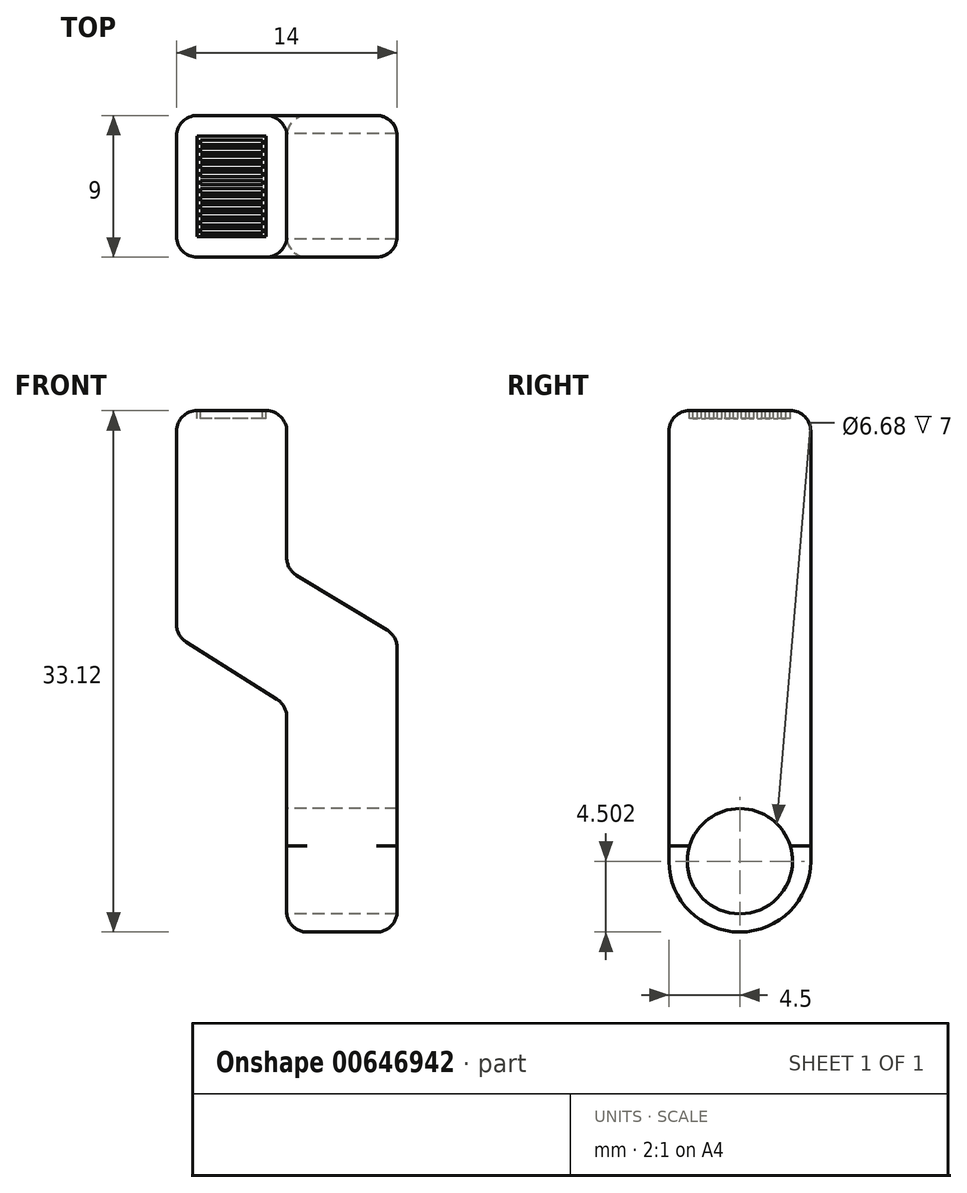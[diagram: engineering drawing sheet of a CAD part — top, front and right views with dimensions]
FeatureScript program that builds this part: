
annotation { "Feature Type Name" : "Feature", "Feature Type Description" : "" }
export const myFeature = defineFeature(function(context is Context, id is Id, definition is map)
    precondition{}
    {
        {
            var Q0;
            Q0=qCreatedBy(makeId("Right.planeOp"),FACE);
            var sketch = newSketch(context, id + "F0", { "sketchPlane" : qUnion([Q0])});
            skLineSegment(sketch, "E0.top", {"start": v(4.5, 14.3) * mm, "end": v(-4.5, 14.3) * mm});
            skLineSegment(sketch, "E0.left", {"start": v(4.5, -14.3) * mm, "end": v(4.5, 14.3) * mm});
            skLineSegment(sketch, "E0.right", {"start": v(-4.5, -14.3) * mm, "end": v(-4.5, 14.3) * mm});
            skPoint(sketch, "E0.middle", {"position": v(0, 0) * mm});
            skArc(sketch, "E1", {"start": v(-4.5, -14.3) * mm, "mid": v(0, -18.8) * mm, "end": v(4.5, -14.3) * mm});
            skCircle(sketch, "E2", {"center": v(0, -14.3) * mm, "radius": 3.34 * mm});
            skSolve(sketch);
        }
        {
            var Q0;
            Q0=makeQuery(id+"F0.imprint","IMPRINT",FACE,{"disambiguationData":[TD([[makeQuery(id+"F0.imprint","IMPRINT",EDGE,{"derivedFrom":sQuery(id+"F0.wireOp",EDGE,"E0.top")}),1.0]])]});
            var Q1;
            {var subQ0=sQuery(id+"F0.wireOp",EDGE,"e674e8e1-4115-40f2-bbbb-998aa0e4564f.121.0");Q1=makeQuery(id+"F0.imprint","IMPRINT",FACE,{"disambiguationData":[TD([[makeQuery(id+"F0.imprint","IMPRINT",EDGE,{"derivedFrom":subQ0}),1.0]])]});}
            var Q2;
            {var subQ0=sQuery(id+"F0.wireOp",EDGE,"e674e8e1-4115-40f2-bbbb-998aa0e4564f.120.0");Q2=makeQuery(id+"F0.imprint","IMPRINT",FACE,{"disambiguationData":[TD([[makeQuery(id+"F0.imprint","IMPRINT",EDGE,{"derivedFrom":subQ0}),1.0]])]});}
            var Q3;
            {var subQ0=sQuery(id+"F0.wireOp",EDGE,"e674e8e1-4115-40f2-bbbb-998aa0e4564f.118.0");Q3=makeQuery(id+"F0.imprint","IMPRINT",FACE,{"disambiguationData":[TD([[makeQuery(id+"F0.imprint","IMPRINT",EDGE,{"derivedFrom":subQ0}),1.0]])]});}
            var Q4;
            {var subQ0=sQuery(id+"F0.wireOp",EDGE,"e674e8e1-4115-40f2-bbbb-998aa0e4564f.119.0");Q4=makeQuery(id+"F0.imprint","IMPRINT",FACE,{"disambiguationData":[TD([[makeQuery(id+"F0.imprint","IMPRINT",EDGE,{"derivedFrom":subQ0}),1.0]])]});}
            var Q5;
            {var subQ0=sQuery(id+"F0.wireOp",EDGE,"e674e8e1-4115-40f2-bbbb-998aa0e4564f.117.0");Q5=makeQuery(id+"F0.imprint","IMPRINT",FACE,{"disambiguationData":[TD([[makeQuery(id+"F0.imprint","IMPRINT",EDGE,{"derivedFrom":subQ0}),1.0]])]});}
            var Q6;
            {var subQ0=sQuery(id+"F0.wireOp",EDGE,"e674e8e1-4115-40f2-bbbb-998aa0e4564f.115.0");Q6=makeQuery(id+"F0.imprint","IMPRINT",FACE,{"disambiguationData":[TD([[makeQuery(id+"F0.imprint","IMPRINT",EDGE,{"derivedFrom":subQ0}),1.0]])]});}
            var Q7;
            {var subQ0=sQuery(id+"F0.wireOp",EDGE,"e674e8e1-4115-40f2-bbbb-998aa0e4564f.116.0");Q7=makeQuery(id+"F0.imprint","IMPRINT",FACE,{"disambiguationData":[TD([[makeQuery(id+"F0.imprint","IMPRINT",EDGE,{"derivedFrom":subQ0}),1.0]])]});}
            var Q8;
            {var subQ0=sQuery(id+"F0.wireOp",EDGE,"e674e8e1-4115-40f2-bbbb-998aa0e4564f.114.0");Q8=makeQuery(id+"F0.imprint","IMPRINT",FACE,{"disambiguationData":[TD([[makeQuery(id+"F0.imprint","IMPRINT",EDGE,{"derivedFrom":subQ0}),1.0]])]});}
            var Q9;
            {var subQ0=sQuery(id+"F0.wireOp",EDGE,"e674e8e1-4115-40f2-bbbb-998aa0e4564f.113.0");Q9=makeQuery(id+"F0.imprint","IMPRINT",FACE,{"disambiguationData":[TD([[makeQuery(id+"F0.imprint","IMPRINT",EDGE,{"derivedFrom":subQ0}),1.0]])]});}
            var Q10;
            {var subQ0=sQuery(id+"F0.wireOp",EDGE,"e674e8e1-4115-40f2-bbbb-998aa0e4564f.112.0");Q10=makeQuery(id+"F0.imprint","IMPRINT",FACE,{"disambiguationData":[TD([[makeQuery(id+"F0.imprint","IMPRINT",EDGE,{"derivedFrom":subQ0}),1.0]])]});}
            var Q11;
            {var subQ0=sQuery(id+"F0.wireOp",EDGE,"e674e8e1-4115-40f2-bbbb-998aa0e4564f.111.0");Q11=makeQuery(id+"F0.imprint","IMPRINT",FACE,{"disambiguationData":[TD([[makeQuery(id+"F0.imprint","IMPRINT",EDGE,{"derivedFrom":subQ0}),1.0]])]});}
            var Q12;
            {var subQ0=sQuery(id+"F0.wireOp",EDGE,"e674e8e1-4115-40f2-bbbb-998aa0e4564f.108.0");Q12=makeQuery(id+"F0.imprint","IMPRINT",FACE,{"disambiguationData":[TD([[makeQuery(id+"F0.imprint","IMPRINT",EDGE,{"derivedFrom":subQ0}),1.0]])]});}
            var Q13;
            {var subQ0=sQuery(id+"F0.wireOp",EDGE,"e674e8e1-4115-40f2-bbbb-998aa0e4564f.106.0");Q13=makeQuery(id+"F0.imprint","IMPRINT",FACE,{"disambiguationData":[TD([[makeQuery(id+"F0.imprint","IMPRINT",EDGE,{"derivedFrom":subQ0}),1.0]])]});}
            var Q14;
            {var subQ0=sQuery(id+"F0.wireOp",EDGE,"e674e8e1-4115-40f2-bbbb-998aa0e4564f.107.0");Q14=makeQuery(id+"F0.imprint","IMPRINT",FACE,{"disambiguationData":[TD([[makeQuery(id+"F0.imprint","IMPRINT",EDGE,{"derivedFrom":subQ0}),1.0]])]});}
            var Q15;
            {var subQ0=sQuery(id+"F0.wireOp",EDGE,"e674e8e1-4115-40f2-bbbb-998aa0e4564f.110.0");Q15=makeQuery(id+"F0.imprint","IMPRINT",FACE,{"disambiguationData":[TD([[makeQuery(id+"F0.imprint","IMPRINT",EDGE,{"derivedFrom":subQ0}),1.0]])]});}
            var Q16;
            {var subQ0=sQuery(id+"F0.wireOp",EDGE,"e674e8e1-4115-40f2-bbbb-998aa0e4564f.109.0");Q16=makeQuery(id+"F0.imprint","IMPRINT",FACE,{"disambiguationData":[TD([[makeQuery(id+"F0.imprint","IMPRINT",EDGE,{"derivedFrom":subQ0}),1.0]])]});}
            var Q17;
            {var subQ0=sQuery(id+"F0.wireOp",EDGE,"e674e8e1-4115-40f2-bbbb-998aa0e4564f.103.0");Q17=makeQuery(id+"F0.imprint","IMPRINT",FACE,{"disambiguationData":[TD([[makeQuery(id+"F0.imprint","IMPRINT",EDGE,{"derivedFrom":subQ0}),1.0]])]});}
            var Q18;
            {var subQ0=sQuery(id+"F0.wireOp",EDGE,"e674e8e1-4115-40f2-bbbb-998aa0e4564f.100.0");Q18=makeQuery(id+"F0.imprint","IMPRINT",FACE,{"disambiguationData":[TD([[makeQuery(id+"F0.imprint","IMPRINT",EDGE,{"derivedFrom":subQ0}),1.0]])]});}
            var Q19;
            {var subQ0=sQuery(id+"F0.wireOp",EDGE,"e674e8e1-4115-40f2-bbbb-998aa0e4564f.98.0");Q19=makeQuery(id+"F0.imprint","IMPRINT",FACE,{"disambiguationData":[TD([[makeQuery(id+"F0.imprint","IMPRINT",EDGE,{"derivedFrom":subQ0}),1.0]])]});}
            var Q20;
            {var subQ0=sQuery(id+"F0.wireOp",EDGE,"e674e8e1-4115-40f2-bbbb-998aa0e4564f.99.0");Q20=makeQuery(id+"F0.imprint","IMPRINT",FACE,{"disambiguationData":[TD([[makeQuery(id+"F0.imprint","IMPRINT",EDGE,{"derivedFrom":subQ0}),1.0]])]});}
            var Q21;
            {var subQ0=sQuery(id+"F0.wireOp",EDGE,"e674e8e1-4115-40f2-bbbb-998aa0e4564f.101.0");Q21=makeQuery(id+"F0.imprint","IMPRINT",FACE,{"disambiguationData":[TD([[makeQuery(id+"F0.imprint","IMPRINT",EDGE,{"derivedFrom":subQ0}),1.0]])]});}
            var Q22;
            {var subQ0=sQuery(id+"F0.wireOp",EDGE,"e674e8e1-4115-40f2-bbbb-998aa0e4564f.102.0");Q22=makeQuery(id+"F0.imprint","IMPRINT",FACE,{"disambiguationData":[TD([[makeQuery(id+"F0.imprint","IMPRINT",EDGE,{"derivedFrom":subQ0}),1.0]])]});}
            var Q23;
            {var subQ0=sQuery(id+"F0.wireOp",EDGE,"e674e8e1-4115-40f2-bbbb-998aa0e4564f.104.0");Q23=makeQuery(id+"F0.imprint","IMPRINT",FACE,{"disambiguationData":[TD([[makeQuery(id+"F0.imprint","IMPRINT",EDGE,{"derivedFrom":subQ0}),1.0]])]});}
            var Q24;
            {var subQ0=sQuery(id+"F0.wireOp",EDGE,"e674e8e1-4115-40f2-bbbb-998aa0e4564f.105.0");Q24=makeQuery(id+"F0.imprint","IMPRINT",FACE,{"disambiguationData":[TD([[makeQuery(id+"F0.imprint","IMPRINT",EDGE,{"derivedFrom":subQ0}),1.0]])]});}
            var Q25;
            {var subQ0=sQuery(id+"F0.wireOp",EDGE,"e674e8e1-4115-40f2-bbbb-998aa0e4564f.92.0");Q25=makeQuery(id+"F0.imprint","IMPRINT",FACE,{"disambiguationData":[TD([[makeQuery(id+"F0.imprint","IMPRINT",EDGE,{"derivedFrom":subQ0}),1.0]])]});}
            var Q26;
            {var subQ0=sQuery(id+"F0.wireOp",EDGE,"e674e8e1-4115-40f2-bbbb-998aa0e4564f.91.0");Q26=makeQuery(id+"F0.imprint","IMPRINT",FACE,{"disambiguationData":[TD([[makeQuery(id+"F0.imprint","IMPRINT",EDGE,{"derivedFrom":subQ0}),1.0]])]});}
            var Q27;
            {var subQ0=sQuery(id+"F0.wireOp",EDGE,"e674e8e1-4115-40f2-bbbb-998aa0e4564f.93.0");Q27=makeQuery(id+"F0.imprint","IMPRINT",FACE,{"disambiguationData":[TD([[makeQuery(id+"F0.imprint","IMPRINT",EDGE,{"derivedFrom":subQ0}),1.0]])]});}
            var Q28;
            {var subQ0=sQuery(id+"F0.wireOp",EDGE,"e674e8e1-4115-40f2-bbbb-998aa0e4564f.94.0");Q28=makeQuery(id+"F0.imprint","IMPRINT",FACE,{"disambiguationData":[TD([[makeQuery(id+"F0.imprint","IMPRINT",EDGE,{"derivedFrom":subQ0}),1.0]])]});}
            var Q29;
            {var subQ0=sQuery(id+"F0.wireOp",EDGE,"e674e8e1-4115-40f2-bbbb-998aa0e4564f.95.0");Q29=makeQuery(id+"F0.imprint","IMPRINT",FACE,{"disambiguationData":[TD([[makeQuery(id+"F0.imprint","IMPRINT",EDGE,{"derivedFrom":subQ0}),1.0]])]});}
            var Q30;
            {var subQ0=sQuery(id+"F0.wireOp",EDGE,"e674e8e1-4115-40f2-bbbb-998aa0e4564f.96.0");Q30=makeQuery(id+"F0.imprint","IMPRINT",FACE,{"disambiguationData":[TD([[makeQuery(id+"F0.imprint","IMPRINT",EDGE,{"derivedFrom":subQ0}),1.0]])]});}
            var Q31;
            {var subQ0=sQuery(id+"F0.wireOp",EDGE,"e674e8e1-4115-40f2-bbbb-998aa0e4564f.97.0");Q31=makeQuery(id+"F0.imprint","IMPRINT",FACE,{"disambiguationData":[TD([[makeQuery(id+"F0.imprint","IMPRINT",EDGE,{"derivedFrom":subQ0}),1.0]])]});}
            var Q32;
            {var subQ0=sQuery(id+"F0.wireOp",EDGE,"e674e8e1-4115-40f2-bbbb-998aa0e4564f.90.0");Q32=makeQuery(id+"F0.imprint","IMPRINT",FACE,{"disambiguationData":[TD([[makeQuery(id+"F0.imprint","IMPRINT",EDGE,{"derivedFrom":subQ0}),1.0]])]});}
            var Q33;
            {var subQ0=sQuery(id+"F0.wireOp",EDGE,"e674e8e1-4115-40f2-bbbb-998aa0e4564f.89.0");Q33=makeQuery(id+"F0.imprint","IMPRINT",FACE,{"disambiguationData":[TD([[makeQuery(id+"F0.imprint","IMPRINT",EDGE,{"derivedFrom":subQ0}),1.0]])]});}
            var Q34;
            {var subQ0=sQuery(id+"F0.wireOp",EDGE,"e674e8e1-4115-40f2-bbbb-998aa0e4564f.88.0");Q34=makeQuery(id+"F0.imprint","IMPRINT",FACE,{"disambiguationData":[TD([[makeQuery(id+"F0.imprint","IMPRINT",EDGE,{"derivedFrom":subQ0}),1.0]])]});}
            var Q35;
            {var subQ0=sQuery(id+"F0.wireOp",EDGE,"e674e8e1-4115-40f2-bbbb-998aa0e4564f.87.0");Q35=makeQuery(id+"F0.imprint","IMPRINT",FACE,{"disambiguationData":[TD([[makeQuery(id+"F0.imprint","IMPRINT",EDGE,{"derivedFrom":subQ0}),1.0]])]});}
            var Q36;
            {var subQ0=sQuery(id+"F0.wireOp",EDGE,"e674e8e1-4115-40f2-bbbb-998aa0e4564f.86.0");Q36=makeQuery(id+"F0.imprint","IMPRINT",FACE,{"disambiguationData":[TD([[makeQuery(id+"F0.imprint","IMPRINT",EDGE,{"derivedFrom":subQ0}),1.0]])]});}
            var Q37;
            {var subQ0=sQuery(id+"F0.wireOp",EDGE,"e674e8e1-4115-40f2-bbbb-998aa0e4564f.85.0");Q37=makeQuery(id+"F0.imprint","IMPRINT",FACE,{"disambiguationData":[TD([[makeQuery(id+"F0.imprint","IMPRINT",EDGE,{"derivedFrom":subQ0}),1.0]])]});}
            var Q38;
            {var subQ0=sQuery(id+"F0.wireOp",EDGE,"e674e8e1-4115-40f2-bbbb-998aa0e4564f.84.0");Q38=makeQuery(id+"F0.imprint","IMPRINT",FACE,{"disambiguationData":[TD([[makeQuery(id+"F0.imprint","IMPRINT",EDGE,{"derivedFrom":subQ0}),1.0]])]});}
            var Q39;
            {var subQ0=sQuery(id+"F0.wireOp",EDGE,"e674e8e1-4115-40f2-bbbb-998aa0e4564f.83.0");Q39=makeQuery(id+"F0.imprint","IMPRINT",FACE,{"disambiguationData":[TD([[makeQuery(id+"F0.imprint","IMPRINT",EDGE,{"derivedFrom":subQ0}),1.0]])]});}
            var Q40;
            {var subQ0=sQuery(id+"F0.wireOp",EDGE,"e674e8e1-4115-40f2-bbbb-998aa0e4564f.82.0");Q40=makeQuery(id+"F0.imprint","IMPRINT",FACE,{"disambiguationData":[TD([[makeQuery(id+"F0.imprint","IMPRINT",EDGE,{"derivedFrom":subQ0}),1.0]])]});}
            var Q41;
            {var subQ0=sQuery(id+"F0.wireOp",EDGE,"e674e8e1-4115-40f2-bbbb-998aa0e4564f.81.0");Q41=makeQuery(id+"F0.imprint","IMPRINT",FACE,{"disambiguationData":[TD([[makeQuery(id+"F0.imprint","IMPRINT",EDGE,{"derivedFrom":subQ0}),1.0]])]});}
            var Q42;
            {var subQ0=sQuery(id+"F0.wireOp",EDGE,"e674e8e1-4115-40f2-bbbb-998aa0e4564f.80.0");Q42=makeQuery(id+"F0.imprint","IMPRINT",FACE,{"disambiguationData":[TD([[makeQuery(id+"F0.imprint","IMPRINT",EDGE,{"derivedFrom":subQ0}),1.0]])]});}
            var Q43;
            {var subQ0=sQuery(id+"F0.wireOp",EDGE,"e674e8e1-4115-40f2-bbbb-998aa0e4564f.79.0");Q43=makeQuery(id+"F0.imprint","IMPRINT",FACE,{"disambiguationData":[TD([[makeQuery(id+"F0.imprint","IMPRINT",EDGE,{"derivedFrom":subQ0}),1.0]])]});}
            var Q44;
            {var subQ0=sQuery(id+"F0.wireOp",EDGE,"e674e8e1-4115-40f2-bbbb-998aa0e4564f.78.0");Q44=makeQuery(id+"F0.imprint","IMPRINT",FACE,{"disambiguationData":[TD([[makeQuery(id+"F0.imprint","IMPRINT",EDGE,{"derivedFrom":subQ0}),1.0]])]});}
            var Q45;
            {var subQ0=sQuery(id+"F0.wireOp",EDGE,"e674e8e1-4115-40f2-bbbb-998aa0e4564f.77.0");Q45=makeQuery(id+"F0.imprint","IMPRINT",FACE,{"disambiguationData":[TD([[makeQuery(id+"F0.imprint","IMPRINT",EDGE,{"derivedFrom":subQ0}),1.0]])]});}
            var Q46;
            {var subQ0=sQuery(id+"F0.wireOp",EDGE,"e674e8e1-4115-40f2-bbbb-998aa0e4564f.76.0");Q46=makeQuery(id+"F0.imprint","IMPRINT",FACE,{"disambiguationData":[TD([[makeQuery(id+"F0.imprint","IMPRINT",EDGE,{"derivedFrom":subQ0}),1.0]])]});}
            var Q47;
            {var subQ0=sQuery(id+"F0.wireOp",EDGE,"e674e8e1-4115-40f2-bbbb-998aa0e4564f.75.0");Q47=makeQuery(id+"F0.imprint","IMPRINT",FACE,{"disambiguationData":[TD([[makeQuery(id+"F0.imprint","IMPRINT",EDGE,{"derivedFrom":subQ0}),1.0]])]});}
            var Q48;
            {var subQ0=sQuery(id+"F0.wireOp",EDGE,"e674e8e1-4115-40f2-bbbb-998aa0e4564f.74.0");Q48=makeQuery(id+"F0.imprint","IMPRINT",FACE,{"disambiguationData":[TD([[makeQuery(id+"F0.imprint","IMPRINT",EDGE,{"derivedFrom":subQ0}),1.0]])]});}
            var Q49;
            {var subQ0=sQuery(id+"F0.wireOp",EDGE,"e674e8e1-4115-40f2-bbbb-998aa0e4564f.73.0");Q49=makeQuery(id+"F0.imprint","IMPRINT",FACE,{"disambiguationData":[TD([[makeQuery(id+"F0.imprint","IMPRINT",EDGE,{"derivedFrom":subQ0}),1.0]])]});}
            var Q50;
            {var subQ0=sQuery(id+"F0.wireOp",EDGE,"e674e8e1-4115-40f2-bbbb-998aa0e4564f.72.0");Q50=makeQuery(id+"F0.imprint","IMPRINT",FACE,{"disambiguationData":[TD([[makeQuery(id+"F0.imprint","IMPRINT",EDGE,{"derivedFrom":subQ0}),1.0]])]});}
            var Q51;
            {var subQ0=sQuery(id+"F0.wireOp",EDGE,"e674e8e1-4115-40f2-bbbb-998aa0e4564f.71.0");Q51=makeQuery(id+"F0.imprint","IMPRINT",FACE,{"disambiguationData":[TD([[makeQuery(id+"F0.imprint","IMPRINT",EDGE,{"derivedFrom":subQ0}),1.0]])]});}
            var Q52;
            {var subQ0=sQuery(id+"F0.wireOp",EDGE,"e674e8e1-4115-40f2-bbbb-998aa0e4564f.70.0");Q52=makeQuery(id+"F0.imprint","IMPRINT",FACE,{"disambiguationData":[TD([[makeQuery(id+"F0.imprint","IMPRINT",EDGE,{"derivedFrom":subQ0}),1.0]])]});}
            var Q53;
            {var subQ0=sQuery(id+"F0.wireOp",EDGE,"e674e8e1-4115-40f2-bbbb-998aa0e4564f.69.0");Q53=makeQuery(id+"F0.imprint","IMPRINT",FACE,{"disambiguationData":[TD([[makeQuery(id+"F0.imprint","IMPRINT",EDGE,{"derivedFrom":subQ0}),1.0]])]});}
            var Q54;
            {var subQ0=sQuery(id+"F0.wireOp",EDGE,"e674e8e1-4115-40f2-bbbb-998aa0e4564f.68.0");Q54=makeQuery(id+"F0.imprint","IMPRINT",FACE,{"disambiguationData":[TD([[makeQuery(id+"F0.imprint","IMPRINT",EDGE,{"derivedFrom":subQ0}),1.0]])]});}
            var Q55;
            {var subQ0=sQuery(id+"F0.wireOp",EDGE,"e674e8e1-4115-40f2-bbbb-998aa0e4564f.67.0");Q55=makeQuery(id+"F0.imprint","IMPRINT",FACE,{"disambiguationData":[TD([[makeQuery(id+"F0.imprint","IMPRINT",EDGE,{"derivedFrom":subQ0}),1.0]])]});}
            var Q56;
            {var subQ0=sQuery(id+"F0.wireOp",EDGE,"e674e8e1-4115-40f2-bbbb-998aa0e4564f.66.0");Q56=makeQuery(id+"F0.imprint","IMPRINT",FACE,{"disambiguationData":[TD([[makeQuery(id+"F0.imprint","IMPRINT",EDGE,{"derivedFrom":subQ0}),1.0]])]});}
            var Q57;
            {var subQ0=sQuery(id+"F0.wireOp",EDGE,"e674e8e1-4115-40f2-bbbb-998aa0e4564f.65.0");Q57=makeQuery(id+"F0.imprint","IMPRINT",FACE,{"disambiguationData":[TD([[makeQuery(id+"F0.imprint","IMPRINT",EDGE,{"derivedFrom":subQ0}),1.0]])]});}
            var Q58;
            {var subQ0=sQuery(id+"F0.wireOp",EDGE,"e674e8e1-4115-40f2-bbbb-998aa0e4564f.64.0");Q58=makeQuery(id+"F0.imprint","IMPRINT",FACE,{"disambiguationData":[TD([[makeQuery(id+"F0.imprint","IMPRINT",EDGE,{"derivedFrom":subQ0}),1.0]])]});}
            var Q59;
            {var subQ0=sQuery(id+"F0.wireOp",EDGE,"e674e8e1-4115-40f2-bbbb-998aa0e4564f.62.0");Q59=makeQuery(id+"F0.imprint","IMPRINT",FACE,{"disambiguationData":[TD([[makeQuery(id+"F0.imprint","IMPRINT",EDGE,{"derivedFrom":subQ0}),1.0]])]});}
            var Q60;
            {var subQ0=sQuery(id+"F0.wireOp",EDGE,"e674e8e1-4115-40f2-bbbb-998aa0e4564f.63.0");Q60=makeQuery(id+"F0.imprint","IMPRINT",FACE,{"disambiguationData":[TD([[makeQuery(id+"F0.imprint","IMPRINT",EDGE,{"derivedFrom":subQ0}),1.0]])]});}
            var Q61;
            {var subQ0=sQuery(id+"F0.wireOp",EDGE,"e674e8e1-4115-40f2-bbbb-998aa0e4564f.61.0");Q61=makeQuery(id+"F0.imprint","IMPRINT",FACE,{"disambiguationData":[TD([[makeQuery(id+"F0.imprint","IMPRINT",EDGE,{"derivedFrom":subQ0}),1.0]])]});}
            var Q62;
            {var subQ0=sQuery(id+"F0.wireOp",EDGE,"e674e8e1-4115-40f2-bbbb-998aa0e4564f.58.0");Q62=makeQuery(id+"F0.imprint","IMPRINT",FACE,{"disambiguationData":[TD([[makeQuery(id+"F0.imprint","IMPRINT",EDGE,{"derivedFrom":subQ0}),1.0]])]});}
            var Q63;
            {var subQ0=sQuery(id+"F0.wireOp",EDGE,"e674e8e1-4115-40f2-bbbb-998aa0e4564f.59.0");Q63=makeQuery(id+"F0.imprint","IMPRINT",FACE,{"disambiguationData":[TD([[makeQuery(id+"F0.imprint","IMPRINT",EDGE,{"derivedFrom":subQ0}),1.0]])]});}
            var Q64;
            {var subQ0=sQuery(id+"F0.wireOp",EDGE,"e674e8e1-4115-40f2-bbbb-998aa0e4564f.60.0");Q64=makeQuery(id+"F0.imprint","IMPRINT",FACE,{"disambiguationData":[TD([[makeQuery(id+"F0.imprint","IMPRINT",EDGE,{"derivedFrom":subQ0}),1.0]])]});}
            var Q65;
            {var subQ0=sQuery(id+"F0.wireOp",EDGE,"e674e8e1-4115-40f2-bbbb-998aa0e4564f.56.0");Q65=makeQuery(id+"F0.imprint","IMPRINT",FACE,{"disambiguationData":[TD([[makeQuery(id+"F0.imprint","IMPRINT",EDGE,{"derivedFrom":subQ0}),1.0]])]});}
            var Q66;
            {var subQ0=sQuery(id+"F0.wireOp",EDGE,"e674e8e1-4115-40f2-bbbb-998aa0e4564f.57.0");Q66=makeQuery(id+"F0.imprint","IMPRINT",FACE,{"disambiguationData":[TD([[makeQuery(id+"F0.imprint","IMPRINT",EDGE,{"derivedFrom":subQ0}),1.0]])]});}
            var Q67;
            {var subQ0=sQuery(id+"F0.wireOp",EDGE,"e674e8e1-4115-40f2-bbbb-998aa0e4564f.55.0");Q67=makeQuery(id+"F0.imprint","IMPRINT",FACE,{"disambiguationData":[TD([[makeQuery(id+"F0.imprint","IMPRINT",EDGE,{"derivedFrom":subQ0}),1.0]])]});}
            var Q68;
            {var subQ0=sQuery(id+"F0.wireOp",EDGE,"e674e8e1-4115-40f2-bbbb-998aa0e4564f.54.0");Q68=makeQuery(id+"F0.imprint","IMPRINT",FACE,{"disambiguationData":[TD([[makeQuery(id+"F0.imprint","IMPRINT",EDGE,{"derivedFrom":subQ0}),1.0]])]});}
            var Q69;
            {var subQ0=sQuery(id+"F0.wireOp",EDGE,"e674e8e1-4115-40f2-bbbb-998aa0e4564f.53.0");Q69=makeQuery(id+"F0.imprint","IMPRINT",FACE,{"disambiguationData":[TD([[makeQuery(id+"F0.imprint","IMPRINT",EDGE,{"derivedFrom":subQ0}),1.0]])]});}
            var Q70;
            {var subQ0=sQuery(id+"F0.wireOp",EDGE,"e674e8e1-4115-40f2-bbbb-998aa0e4564f.52.0");Q70=makeQuery(id+"F0.imprint","IMPRINT",FACE,{"disambiguationData":[TD([[makeQuery(id+"F0.imprint","IMPRINT",EDGE,{"derivedFrom":subQ0}),1.0]])]});}
            var Q71;
            {var subQ0=sQuery(id+"F0.wireOp",EDGE,"e674e8e1-4115-40f2-bbbb-998aa0e4564f.51.0");Q71=makeQuery(id+"F0.imprint","IMPRINT",FACE,{"disambiguationData":[TD([[makeQuery(id+"F0.imprint","IMPRINT",EDGE,{"derivedFrom":subQ0}),1.0]])]});}
            var Q72;
            {var subQ0=sQuery(id+"F0.wireOp",EDGE,"e674e8e1-4115-40f2-bbbb-998aa0e4564f.50.0");Q72=makeQuery(id+"F0.imprint","IMPRINT",FACE,{"disambiguationData":[TD([[makeQuery(id+"F0.imprint","IMPRINT",EDGE,{"derivedFrom":subQ0}),1.0]])]});}
            var Q73;
            {var subQ0=sQuery(id+"F0.wireOp",EDGE,"e674e8e1-4115-40f2-bbbb-998aa0e4564f.49.0");Q73=makeQuery(id+"F0.imprint","IMPRINT",FACE,{"disambiguationData":[TD([[makeQuery(id+"F0.imprint","IMPRINT",EDGE,{"derivedFrom":subQ0}),1.0]])]});}
            var Q74;
            {var subQ0=sQuery(id+"F0.wireOp",EDGE,"e674e8e1-4115-40f2-bbbb-998aa0e4564f.48.0");Q74=makeQuery(id+"F0.imprint","IMPRINT",FACE,{"disambiguationData":[TD([[makeQuery(id+"F0.imprint","IMPRINT",EDGE,{"derivedFrom":subQ0}),1.0]])]});}
            var Q75;
            {var subQ0=sQuery(id+"F0.wireOp",EDGE,"e674e8e1-4115-40f2-bbbb-998aa0e4564f.47.0");Q75=makeQuery(id+"F0.imprint","IMPRINT",FACE,{"disambiguationData":[TD([[makeQuery(id+"F0.imprint","IMPRINT",EDGE,{"derivedFrom":subQ0}),1.0]])]});}
            var Q76;
            {var subQ0=sQuery(id+"F0.wireOp",EDGE,"e674e8e1-4115-40f2-bbbb-998aa0e4564f.44.0");Q76=makeQuery(id+"F0.imprint","IMPRINT",FACE,{"disambiguationData":[TD([[makeQuery(id+"F0.imprint","IMPRINT",EDGE,{"derivedFrom":subQ0}),1.0]])]});}
            var Q77;
            {var subQ0=sQuery(id+"F0.wireOp",EDGE,"e674e8e1-4115-40f2-bbbb-998aa0e4564f.46.0");Q77=makeQuery(id+"F0.imprint","IMPRINT",FACE,{"disambiguationData":[TD([[makeQuery(id+"F0.imprint","IMPRINT",EDGE,{"derivedFrom":subQ0}),1.0]])]});}
            var Q78;
            {var subQ0=sQuery(id+"F0.wireOp",EDGE,"e674e8e1-4115-40f2-bbbb-998aa0e4564f.43.0");Q78=makeQuery(id+"F0.imprint","IMPRINT",FACE,{"disambiguationData":[TD([[makeQuery(id+"F0.imprint","IMPRINT",EDGE,{"derivedFrom":subQ0}),1.0]])]});}
            var Q79;
            {var subQ0=sQuery(id+"F0.wireOp",EDGE,"e674e8e1-4115-40f2-bbbb-998aa0e4564f.45.0");Q79=makeQuery(id+"F0.imprint","IMPRINT",FACE,{"disambiguationData":[TD([[makeQuery(id+"F0.imprint","IMPRINT",EDGE,{"derivedFrom":subQ0}),1.0]])]});}
            var Q80;
            {var subQ0=sQuery(id+"F0.wireOp",EDGE,"e674e8e1-4115-40f2-bbbb-998aa0e4564f.42.0");Q80=makeQuery(id+"F0.imprint","IMPRINT",FACE,{"disambiguationData":[TD([[makeQuery(id+"F0.imprint","IMPRINT",EDGE,{"derivedFrom":subQ0}),1.0]])]});}
            var Q81;
            {var subQ0=sQuery(id+"F0.wireOp",EDGE,"e674e8e1-4115-40f2-bbbb-998aa0e4564f.41.0");Q81=makeQuery(id+"F0.imprint","IMPRINT",FACE,{"disambiguationData":[TD([[makeQuery(id+"F0.imprint","IMPRINT",EDGE,{"derivedFrom":subQ0}),1.0]])]});}
            var Q82;
            {var subQ0=sQuery(id+"F0.wireOp",EDGE,"e674e8e1-4115-40f2-bbbb-998aa0e4564f.40.0");Q82=makeQuery(id+"F0.imprint","IMPRINT",FACE,{"disambiguationData":[TD([[makeQuery(id+"F0.imprint","IMPRINT",EDGE,{"derivedFrom":subQ0}),1.0]])]});}
            var Q83;
            {var subQ0=sQuery(id+"F0.wireOp",EDGE,"e674e8e1-4115-40f2-bbbb-998aa0e4564f.39.0");Q83=makeQuery(id+"F0.imprint","IMPRINT",FACE,{"disambiguationData":[TD([[makeQuery(id+"F0.imprint","IMPRINT",EDGE,{"derivedFrom":subQ0}),1.0]])]});}
            var Q84;
            {var subQ0=sQuery(id+"F0.wireOp",EDGE,"e674e8e1-4115-40f2-bbbb-998aa0e4564f.35.0");Q84=makeQuery(id+"F0.imprint","IMPRINT",FACE,{"disambiguationData":[TD([[makeQuery(id+"F0.imprint","IMPRINT",EDGE,{"derivedFrom":subQ0}),1.0]])]});}
            var Q85;
            {var subQ0=sQuery(id+"F0.wireOp",EDGE,"e674e8e1-4115-40f2-bbbb-998aa0e4564f.38.0");Q85=makeQuery(id+"F0.imprint","IMPRINT",FACE,{"disambiguationData":[TD([[makeQuery(id+"F0.imprint","IMPRINT",EDGE,{"derivedFrom":subQ0}),1.0]])]});}
            var Q86;
            {var subQ0=sQuery(id+"F0.wireOp",EDGE,"e674e8e1-4115-40f2-bbbb-998aa0e4564f.34.0");Q86=makeQuery(id+"F0.imprint","IMPRINT",FACE,{"disambiguationData":[TD([[makeQuery(id+"F0.imprint","IMPRINT",EDGE,{"derivedFrom":subQ0}),1.0]])]});}
            var Q87;
            {var subQ0=sQuery(id+"F0.wireOp",EDGE,"e674e8e1-4115-40f2-bbbb-998aa0e4564f.37.0");Q87=makeQuery(id+"F0.imprint","IMPRINT",FACE,{"disambiguationData":[TD([[makeQuery(id+"F0.imprint","IMPRINT",EDGE,{"derivedFrom":subQ0}),1.0]])]});}
            var Q88;
            {var subQ0=sQuery(id+"F0.wireOp",EDGE,"e674e8e1-4115-40f2-bbbb-998aa0e4564f.36.0");Q88=makeQuery(id+"F0.imprint","IMPRINT",FACE,{"disambiguationData":[TD([[makeQuery(id+"F0.imprint","IMPRINT",EDGE,{"derivedFrom":subQ0}),1.0]])]});}
            var Q89;
            {var subQ0=sQuery(id+"F0.wireOp",EDGE,"e674e8e1-4115-40f2-bbbb-998aa0e4564f.33.0");Q89=makeQuery(id+"F0.imprint","IMPRINT",FACE,{"disambiguationData":[TD([[makeQuery(id+"F0.imprint","IMPRINT",EDGE,{"derivedFrom":subQ0}),1.0]])]});}
            var Q90;
            {var subQ0=sQuery(id+"F0.wireOp",EDGE,"e674e8e1-4115-40f2-bbbb-998aa0e4564f.32.0");Q90=makeQuery(id+"F0.imprint","IMPRINT",FACE,{"disambiguationData":[TD([[makeQuery(id+"F0.imprint","IMPRINT",EDGE,{"derivedFrom":subQ0}),1.0]])]});}
            var Q91;
            {var subQ0=sQuery(id+"F0.wireOp",EDGE,"e674e8e1-4115-40f2-bbbb-998aa0e4564f.30.0");Q91=makeQuery(id+"F0.imprint","IMPRINT",FACE,{"disambiguationData":[TD([[makeQuery(id+"F0.imprint","IMPRINT",EDGE,{"derivedFrom":subQ0}),1.0]])]});}
            var Q92;
            {var subQ0=sQuery(id+"F0.wireOp",EDGE,"e674e8e1-4115-40f2-bbbb-998aa0e4564f.31.0");Q92=makeQuery(id+"F0.imprint","IMPRINT",FACE,{"disambiguationData":[TD([[makeQuery(id+"F0.imprint","IMPRINT",EDGE,{"derivedFrom":subQ0}),1.0]])]});}
            var Q93;
            {var subQ0=sQuery(id+"F0.wireOp",EDGE,"e674e8e1-4115-40f2-bbbb-998aa0e4564f.29.0");Q93=makeQuery(id+"F0.imprint","IMPRINT",FACE,{"disambiguationData":[TD([[makeQuery(id+"F0.imprint","IMPRINT",EDGE,{"derivedFrom":subQ0}),1.0]])]});}
            var Q94;
            {var subQ0=sQuery(id+"F0.wireOp",EDGE,"e674e8e1-4115-40f2-bbbb-998aa0e4564f.28.0");Q94=makeQuery(id+"F0.imprint","IMPRINT",FACE,{"disambiguationData":[TD([[makeQuery(id+"F0.imprint","IMPRINT",EDGE,{"derivedFrom":subQ0}),1.0]])]});}
            var Q95;
            {var subQ0=sQuery(id+"F0.wireOp",EDGE,"e674e8e1-4115-40f2-bbbb-998aa0e4564f.27.0");Q95=makeQuery(id+"F0.imprint","IMPRINT",FACE,{"disambiguationData":[TD([[makeQuery(id+"F0.imprint","IMPRINT",EDGE,{"derivedFrom":subQ0}),1.0]])]});}
            var Q96;
            {var subQ0=sQuery(id+"F0.wireOp",EDGE,"e674e8e1-4115-40f2-bbbb-998aa0e4564f.26.0");Q96=makeQuery(id+"F0.imprint","IMPRINT",FACE,{"disambiguationData":[TD([[makeQuery(id+"F0.imprint","IMPRINT",EDGE,{"derivedFrom":subQ0}),1.0]])]});}
            var Q97;
            {var subQ0=sQuery(id+"F0.wireOp",EDGE,"e674e8e1-4115-40f2-bbbb-998aa0e4564f.24.0");Q97=makeQuery(id+"F0.imprint","IMPRINT",FACE,{"disambiguationData":[TD([[makeQuery(id+"F0.imprint","IMPRINT",EDGE,{"derivedFrom":subQ0}),1.0]])]});}
            var Q98;
            {var subQ0=sQuery(id+"F0.wireOp",EDGE,"e674e8e1-4115-40f2-bbbb-998aa0e4564f.25.0");Q98=makeQuery(id+"F0.imprint","IMPRINT",FACE,{"disambiguationData":[TD([[makeQuery(id+"F0.imprint","IMPRINT",EDGE,{"derivedFrom":subQ0}),1.0]])]});}
            var Q99;
            {var subQ0=sQuery(id+"F0.wireOp",EDGE,"e674e8e1-4115-40f2-bbbb-998aa0e4564f.23.0");Q99=makeQuery(id+"F0.imprint","IMPRINT",FACE,{"disambiguationData":[TD([[makeQuery(id+"F0.imprint","IMPRINT",EDGE,{"derivedFrom":subQ0}),1.0]])]});}
            var Q100;
            {var subQ0=sQuery(id+"F0.wireOp",EDGE,"e674e8e1-4115-40f2-bbbb-998aa0e4564f.22.0");Q100=makeQuery(id+"F0.imprint","IMPRINT",FACE,{"disambiguationData":[TD([[makeQuery(id+"F0.imprint","IMPRINT",EDGE,{"derivedFrom":subQ0}),1.0]])]});}
            var Q101;
            {var subQ0=sQuery(id+"F0.wireOp",EDGE,"e674e8e1-4115-40f2-bbbb-998aa0e4564f.21.0");Q101=makeQuery(id+"F0.imprint","IMPRINT",FACE,{"disambiguationData":[TD([[makeQuery(id+"F0.imprint","IMPRINT",EDGE,{"derivedFrom":subQ0}),1.0]])]});}
            var Q102;
            {var subQ0=sQuery(id+"F0.wireOp",EDGE,"e674e8e1-4115-40f2-bbbb-998aa0e4564f.20.0");Q102=makeQuery(id+"F0.imprint","IMPRINT",FACE,{"disambiguationData":[TD([[makeQuery(id+"F0.imprint","IMPRINT",EDGE,{"derivedFrom":subQ0}),1.0]])]});}
            var Q103;
            {var subQ0=sQuery(id+"F0.wireOp",EDGE,"e674e8e1-4115-40f2-bbbb-998aa0e4564f.19.0");Q103=makeQuery(id+"F0.imprint","IMPRINT",FACE,{"disambiguationData":[TD([[makeQuery(id+"F0.imprint","IMPRINT",EDGE,{"derivedFrom":subQ0}),1.0]])]});}
            var Q104;
            {var subQ0=sQuery(id+"F0.wireOp",EDGE,"e674e8e1-4115-40f2-bbbb-998aa0e4564f.18.0");Q104=makeQuery(id+"F0.imprint","IMPRINT",FACE,{"disambiguationData":[TD([[makeQuery(id+"F0.imprint","IMPRINT",EDGE,{"derivedFrom":subQ0}),1.0]])]});}
            var Q105;
            {var subQ0=sQuery(id+"F0.wireOp",EDGE,"e674e8e1-4115-40f2-bbbb-998aa0e4564f.17.0");Q105=makeQuery(id+"F0.imprint","IMPRINT",FACE,{"disambiguationData":[TD([[makeQuery(id+"F0.imprint","IMPRINT",EDGE,{"derivedFrom":subQ0}),1.0]])]});}
            var Q106;
            {var subQ0=sQuery(id+"F0.wireOp",EDGE,"e674e8e1-4115-40f2-bbbb-998aa0e4564f.16.0");Q106=makeQuery(id+"F0.imprint","IMPRINT",FACE,{"disambiguationData":[TD([[makeQuery(id+"F0.imprint","IMPRINT",EDGE,{"derivedFrom":subQ0}),1.0]])]});}
            var Q107;
            {var subQ0=sQuery(id+"F0.wireOp",EDGE,"e674e8e1-4115-40f2-bbbb-998aa0e4564f.15.0");Q107=makeQuery(id+"F0.imprint","IMPRINT",FACE,{"disambiguationData":[TD([[makeQuery(id+"F0.imprint","IMPRINT",EDGE,{"derivedFrom":subQ0}),1.0]])]});}
            var Q108;
            {var subQ0=sQuery(id+"F0.wireOp",EDGE,"e674e8e1-4115-40f2-bbbb-998aa0e4564f.14.0");Q108=makeQuery(id+"F0.imprint","IMPRINT",FACE,{"disambiguationData":[TD([[makeQuery(id+"F0.imprint","IMPRINT",EDGE,{"derivedFrom":subQ0}),1.0]])]});}
            var Q109;
            {var subQ0=sQuery(id+"F0.wireOp",EDGE,"e674e8e1-4115-40f2-bbbb-998aa0e4564f.13.0");Q109=makeQuery(id+"F0.imprint","IMPRINT",FACE,{"disambiguationData":[TD([[makeQuery(id+"F0.imprint","IMPRINT",EDGE,{"derivedFrom":subQ0}),1.0]])]});}
            var Q110;
            {var subQ0=sQuery(id+"F0.wireOp",EDGE,"e674e8e1-4115-40f2-bbbb-998aa0e4564f.12.0");Q110=makeQuery(id+"F0.imprint","IMPRINT",FACE,{"disambiguationData":[TD([[makeQuery(id+"F0.imprint","IMPRINT",EDGE,{"derivedFrom":subQ0}),1.0]])]});}
            var Q111;
            {var subQ0=sQuery(id+"F0.wireOp",EDGE,"e674e8e1-4115-40f2-bbbb-998aa0e4564f.11.0");Q111=makeQuery(id+"F0.imprint","IMPRINT",FACE,{"disambiguationData":[TD([[makeQuery(id+"F0.imprint","IMPRINT",EDGE,{"derivedFrom":subQ0}),1.0]])]});}
            var Q112;
            {var subQ0=sQuery(id+"F0.wireOp",EDGE,"e674e8e1-4115-40f2-bbbb-998aa0e4564f.10.0");Q112=makeQuery(id+"F0.imprint","IMPRINT",FACE,{"disambiguationData":[TD([[makeQuery(id+"F0.imprint","IMPRINT",EDGE,{"derivedFrom":subQ0}),1.0]])]});}
            var Q113;
            {var subQ0=sQuery(id+"F0.wireOp",EDGE,"e674e8e1-4115-40f2-bbbb-998aa0e4564f.9.0");Q113=makeQuery(id+"F0.imprint","IMPRINT",FACE,{"disambiguationData":[TD([[makeQuery(id+"F0.imprint","IMPRINT",EDGE,{"derivedFrom":subQ0}),1.0]])]});}
            var Q114;
            {var subQ0=sQuery(id+"F0.wireOp",EDGE,"e674e8e1-4115-40f2-bbbb-998aa0e4564f.8.0");Q114=makeQuery(id+"F0.imprint","IMPRINT",FACE,{"disambiguationData":[TD([[makeQuery(id+"F0.imprint","IMPRINT",EDGE,{"derivedFrom":subQ0}),1.0]])]});}
            var Q115;
            {var subQ0=sQuery(id+"F0.wireOp",EDGE,"e674e8e1-4115-40f2-bbbb-998aa0e4564f.7.0");Q115=makeQuery(id+"F0.imprint","IMPRINT",FACE,{"disambiguationData":[TD([[makeQuery(id+"F0.imprint","IMPRINT",EDGE,{"derivedFrom":subQ0}),1.0]])]});}
            var Q116;
            {var subQ0=sQuery(id+"F0.wireOp",EDGE,"e674e8e1-4115-40f2-bbbb-998aa0e4564f.6.0");Q116=makeQuery(id+"F0.imprint","IMPRINT",FACE,{"disambiguationData":[TD([[makeQuery(id+"F0.imprint","IMPRINT",EDGE,{"derivedFrom":subQ0}),1.0]])]});}
            var Q117;
            {var subQ0=sQuery(id+"F0.wireOp",EDGE,"e674e8e1-4115-40f2-bbbb-998aa0e4564f.5.0");Q117=makeQuery(id+"F0.imprint","IMPRINT",FACE,{"disambiguationData":[TD([[makeQuery(id+"F0.imprint","IMPRINT",EDGE,{"derivedFrom":subQ0}),1.0]])]});}
            var Q118;
            {var subQ0=sQuery(id+"F0.wireOp",EDGE,"e674e8e1-4115-40f2-bbbb-998aa0e4564f.4.0");Q118=makeQuery(id+"F0.imprint","IMPRINT",FACE,{"disambiguationData":[TD([[makeQuery(id+"F0.imprint","IMPRINT",EDGE,{"derivedFrom":subQ0}),1.0]])]});}
            var Q119;
            {var subQ0=sQuery(id+"F0.wireOp",EDGE,"e674e8e1-4115-40f2-bbbb-998aa0e4564f.3.0");Q119=makeQuery(id+"F0.imprint","IMPRINT",FACE,{"disambiguationData":[TD([[makeQuery(id+"F0.imprint","IMPRINT",EDGE,{"derivedFrom":subQ0}),1.0]])]});}
            var Q120;
            {var subQ0=sQuery(id+"F0.wireOp",EDGE,"e674e8e1-4115-40f2-bbbb-998aa0e4564f.2.0");Q120=makeQuery(id+"F0.imprint","IMPRINT",FACE,{"disambiguationData":[TD([[makeQuery(id+"F0.imprint","IMPRINT",EDGE,{"derivedFrom":subQ0}),1.0]])]});}
            var Q121;
            {var subQ0=sQuery(id+"F0.wireOp",EDGE,"e674e8e1-4115-40f2-bbbb-998aa0e4564f.1.0");Q121=makeQuery(id+"F0.imprint","IMPRINT",FACE,{"disambiguationData":[TD([[makeQuery(id+"F0.imprint","IMPRINT",EDGE,{"derivedFrom":subQ0}),1.0]])]});}
            var Q122;
            {var subQ0=sQuery(id+"F0.wireOp",EDGE,"chszo8gj-8hQ4-lesQ-f9Y4-zgW5iuPWSUHq");Q122=makeQuery(id+"F0.imprint","IMPRINT",FACE,{"disambiguationData":[TD([[makeQuery(id+"F0.imprint","IMPRINT",EDGE,{"derivedFrom":subQ0}),1.0]])]});}
            var Q123;
            {var subQ0=sQuery(id+"F0.wireOp",EDGE,"e674e8e1-4115-40f2-bbbb-998aa0e4564f.149.0");Q123=makeQuery(id+"F0.imprint","IMPRINT",FACE,{"disambiguationData":[TD([[makeQuery(id+"F0.imprint","IMPRINT",EDGE,{"derivedFrom":subQ0}),1.0]])]});}
            var Q124;
            {var subQ0=sQuery(id+"F0.wireOp",EDGE,"e674e8e1-4115-40f2-bbbb-998aa0e4564f.148.0");Q124=makeQuery(id+"F0.imprint","IMPRINT",FACE,{"disambiguationData":[TD([[makeQuery(id+"F0.imprint","IMPRINT",EDGE,{"derivedFrom":subQ0}),1.0]])]});}
            var Q125;
            {var subQ0=sQuery(id+"F0.wireOp",EDGE,"e674e8e1-4115-40f2-bbbb-998aa0e4564f.147.0");Q125=makeQuery(id+"F0.imprint","IMPRINT",FACE,{"disambiguationData":[TD([[makeQuery(id+"F0.imprint","IMPRINT",EDGE,{"derivedFrom":subQ0}),1.0]])]});}
            var Q126;
            {var subQ0=sQuery(id+"F0.wireOp",EDGE,"e674e8e1-4115-40f2-bbbb-998aa0e4564f.146.0");Q126=makeQuery(id+"F0.imprint","IMPRINT",FACE,{"disambiguationData":[TD([[makeQuery(id+"F0.imprint","IMPRINT",EDGE,{"derivedFrom":subQ0}),1.0]])]});}
            var Q127;
            {var subQ0=sQuery(id+"F0.wireOp",EDGE,"e674e8e1-4115-40f2-bbbb-998aa0e4564f.145.0");Q127=makeQuery(id+"F0.imprint","IMPRINT",FACE,{"disambiguationData":[TD([[makeQuery(id+"F0.imprint","IMPRINT",EDGE,{"derivedFrom":subQ0}),1.0]])]});}
            var Q128;
            {var subQ0=sQuery(id+"F0.wireOp",EDGE,"e674e8e1-4115-40f2-bbbb-998aa0e4564f.143.0");Q128=makeQuery(id+"F0.imprint","IMPRINT",FACE,{"disambiguationData":[TD([[makeQuery(id+"F0.imprint","IMPRINT",EDGE,{"derivedFrom":subQ0}),1.0]])]});}
            var Q129;
            {var subQ0=sQuery(id+"F0.wireOp",EDGE,"e674e8e1-4115-40f2-bbbb-998aa0e4564f.144.0");Q129=makeQuery(id+"F0.imprint","IMPRINT",FACE,{"disambiguationData":[TD([[makeQuery(id+"F0.imprint","IMPRINT",EDGE,{"derivedFrom":subQ0}),1.0]])]});}
            var Q130;
            {var subQ0=sQuery(id+"F0.wireOp",EDGE,"e674e8e1-4115-40f2-bbbb-998aa0e4564f.142.0");Q130=makeQuery(id+"F0.imprint","IMPRINT",FACE,{"disambiguationData":[TD([[makeQuery(id+"F0.imprint","IMPRINT",EDGE,{"derivedFrom":subQ0}),1.0]])]});}
            var Q131;
            {var subQ0=sQuery(id+"F0.wireOp",EDGE,"e674e8e1-4115-40f2-bbbb-998aa0e4564f.141.0");Q131=makeQuery(id+"F0.imprint","IMPRINT",FACE,{"disambiguationData":[TD([[makeQuery(id+"F0.imprint","IMPRINT",EDGE,{"derivedFrom":subQ0}),1.0]])]});}
            var Q132;
            {var subQ0=sQuery(id+"F0.wireOp",EDGE,"e674e8e1-4115-40f2-bbbb-998aa0e4564f.139.0");Q132=makeQuery(id+"F0.imprint","IMPRINT",FACE,{"disambiguationData":[TD([[makeQuery(id+"F0.imprint","IMPRINT",EDGE,{"derivedFrom":subQ0}),1.0]])]});}
            var Q133;
            {var subQ0=sQuery(id+"F0.wireOp",EDGE,"e674e8e1-4115-40f2-bbbb-998aa0e4564f.140.0");Q133=makeQuery(id+"F0.imprint","IMPRINT",FACE,{"disambiguationData":[TD([[makeQuery(id+"F0.imprint","IMPRINT",EDGE,{"derivedFrom":subQ0}),1.0]])]});}
            var Q134;
            {var subQ0=sQuery(id+"F0.wireOp",EDGE,"e674e8e1-4115-40f2-bbbb-998aa0e4564f.138.0");Q134=makeQuery(id+"F0.imprint","IMPRINT",FACE,{"disambiguationData":[TD([[makeQuery(id+"F0.imprint","IMPRINT",EDGE,{"derivedFrom":subQ0}),1.0]])]});}
            var Q135;
            {var subQ0=sQuery(id+"F0.wireOp",EDGE,"e674e8e1-4115-40f2-bbbb-998aa0e4564f.137.0");Q135=makeQuery(id+"F0.imprint","IMPRINT",FACE,{"disambiguationData":[TD([[makeQuery(id+"F0.imprint","IMPRINT",EDGE,{"derivedFrom":subQ0}),1.0]])]});}
            var Q136;
            {var subQ0=sQuery(id+"F0.wireOp",EDGE,"e674e8e1-4115-40f2-bbbb-998aa0e4564f.136.0");Q136=makeQuery(id+"F0.imprint","IMPRINT",FACE,{"disambiguationData":[TD([[makeQuery(id+"F0.imprint","IMPRINT",EDGE,{"derivedFrom":subQ0}),1.0]])]});}
            var Q137;
            {var subQ0=sQuery(id+"F0.wireOp",EDGE,"e674e8e1-4115-40f2-bbbb-998aa0e4564f.135.0");Q137=makeQuery(id+"F0.imprint","IMPRINT",FACE,{"disambiguationData":[TD([[makeQuery(id+"F0.imprint","IMPRINT",EDGE,{"derivedFrom":subQ0}),1.0]])]});}
            var Q138;
            {var subQ0=sQuery(id+"F0.wireOp",EDGE,"e674e8e1-4115-40f2-bbbb-998aa0e4564f.133.0");Q138=makeQuery(id+"F0.imprint","IMPRINT",FACE,{"disambiguationData":[TD([[makeQuery(id+"F0.imprint","IMPRINT",EDGE,{"derivedFrom":subQ0}),1.0]])]});}
            var Q139;
            {var subQ0=sQuery(id+"F0.wireOp",EDGE,"e674e8e1-4115-40f2-bbbb-998aa0e4564f.134.0");Q139=makeQuery(id+"F0.imprint","IMPRINT",FACE,{"disambiguationData":[TD([[makeQuery(id+"F0.imprint","IMPRINT",EDGE,{"derivedFrom":subQ0}),1.0]])]});}
            var Q140;
            {var subQ0=sQuery(id+"F0.wireOp",EDGE,"e674e8e1-4115-40f2-bbbb-998aa0e4564f.132.0");Q140=makeQuery(id+"F0.imprint","IMPRINT",FACE,{"disambiguationData":[TD([[makeQuery(id+"F0.imprint","IMPRINT",EDGE,{"derivedFrom":subQ0}),1.0]])]});}
            var Q141;
            {var subQ0=sQuery(id+"F0.wireOp",EDGE,"e674e8e1-4115-40f2-bbbb-998aa0e4564f.131.0");Q141=makeQuery(id+"F0.imprint","IMPRINT",FACE,{"disambiguationData":[TD([[makeQuery(id+"F0.imprint","IMPRINT",EDGE,{"derivedFrom":subQ0}),1.0]])]});}
            var Q142;
            {var subQ0=sQuery(id+"F0.wireOp",EDGE,"e674e8e1-4115-40f2-bbbb-998aa0e4564f.130.0");Q142=makeQuery(id+"F0.imprint","IMPRINT",FACE,{"disambiguationData":[TD([[makeQuery(id+"F0.imprint","IMPRINT",EDGE,{"derivedFrom":subQ0}),1.0]])]});}
            var Q143;
            {var subQ0=sQuery(id+"F0.wireOp",EDGE,"e674e8e1-4115-40f2-bbbb-998aa0e4564f.129.0");Q143=makeQuery(id+"F0.imprint","IMPRINT",FACE,{"disambiguationData":[TD([[makeQuery(id+"F0.imprint","IMPRINT",EDGE,{"derivedFrom":subQ0}),1.0]])]});}
            var Q144;
            {var subQ0=sQuery(id+"F0.wireOp",EDGE,"e674e8e1-4115-40f2-bbbb-998aa0e4564f.127.0");Q144=makeQuery(id+"F0.imprint","IMPRINT",FACE,{"disambiguationData":[TD([[makeQuery(id+"F0.imprint","IMPRINT",EDGE,{"derivedFrom":subQ0}),1.0]])]});}
            var Q145;
            {var subQ0=sQuery(id+"F0.wireOp",EDGE,"e674e8e1-4115-40f2-bbbb-998aa0e4564f.128.0");Q145=makeQuery(id+"F0.imprint","IMPRINT",FACE,{"disambiguationData":[TD([[makeQuery(id+"F0.imprint","IMPRINT",EDGE,{"derivedFrom":subQ0}),1.0]])]});}
            var Q146;
            {var subQ0=sQuery(id+"F0.wireOp",EDGE,"e674e8e1-4115-40f2-bbbb-998aa0e4564f.126.0");Q146=makeQuery(id+"F0.imprint","IMPRINT",FACE,{"disambiguationData":[TD([[makeQuery(id+"F0.imprint","IMPRINT",EDGE,{"derivedFrom":subQ0}),1.0]])]});}
            var Q147;
            {var subQ0=sQuery(id+"F0.wireOp",EDGE,"e674e8e1-4115-40f2-bbbb-998aa0e4564f.125.0");Q147=makeQuery(id+"F0.imprint","IMPRINT",FACE,{"disambiguationData":[TD([[makeQuery(id+"F0.imprint","IMPRINT",EDGE,{"derivedFrom":subQ0}),1.0]])]});}
            var Q148;
            {var subQ0=sQuery(id+"F0.wireOp",EDGE,"e674e8e1-4115-40f2-bbbb-998aa0e4564f.124.0");Q148=makeQuery(id+"F0.imprint","IMPRINT",FACE,{"disambiguationData":[TD([[makeQuery(id+"F0.imprint","IMPRINT",EDGE,{"derivedFrom":subQ0}),1.0]])]});}
            var Q149;
            {var subQ0=sQuery(id+"F0.wireOp",EDGE,"e674e8e1-4115-40f2-bbbb-998aa0e4564f.123.0");Q149=makeQuery(id+"F0.imprint","IMPRINT",FACE,{"disambiguationData":[TD([[makeQuery(id+"F0.imprint","IMPRINT",EDGE,{"derivedFrom":subQ0}),1.0]])]});}
            var Q150;
            {var subQ0=sQuery(id+"F0.wireOp",EDGE,"e674e8e1-4115-40f2-bbbb-998aa0e4564f.122.0");Q150=makeQuery(id+"F0.imprint","IMPRINT",FACE,{"disambiguationData":[TD([[makeQuery(id+"F0.imprint","IMPRINT",EDGE,{"derivedFrom":subQ0}),1.0]])]});}
            extrude(context, id + "F1", {"entities" : qUnion([Q0, Q1, Q2, Q3, Q4, Q5, Q6, Q7, Q8, Q9, Q10, Q11, Q12, Q13, Q14, Q15, Q16, Q17, Q18, Q19, Q20, Q21, Q22, Q23, Q24, Q25, Q26, Q27, Q28, Q29, Q30, Q31, Q32, Q33, Q34, Q35, Q36, Q37, Q38, Q39, Q40, Q41, Q42, Q43, Q44, Q45, Q46, Q47, Q48, Q49, Q50, Q51, Q52, Q53, Q54, Q55, Q56, Q57, Q58, Q59, Q60, Q61, Q62, Q63, Q64, Q65, Q66, Q67, Q68, Q69, Q70, Q71, Q72, Q73, Q74, Q75, Q76, Q77, Q78, Q79, Q80, Q81, Q82, Q83, Q84, Q85, Q86, Q87, Q88, Q89, Q90, Q91, Q92, Q93, Q94, Q95, Q96, Q97, Q98, Q99, Q100, Q101, Q102, Q103, Q104, Q105, Q106, Q107, Q108, Q109, Q110, Q111, Q112, Q113, Q114, Q115, Q116, Q117, Q118, Q119, Q120, Q121, Q122, Q123, Q124, Q125, Q126, Q127, Q128, Q129, Q130, Q131, Q132, Q133, Q134, Q135, Q136, Q137, Q138, Q139, Q140, Q141, Q142, Q143, Q144, Q145, Q146, Q147, Q148, Q149, Q150]), "depth" : 7 * mm, "offsetDistance" : 25 * mm});
        }
        {
            var Q0;
            Q0=makeQuery(id+"F1.opExtrude","SWEPT_FACE",FACE,{"disambiguationData":[OSD([sQuery(id+"F0.wireOp",EDGE,"E0.right")])]});
            var sketch = newSketch(context, id + "F2", { "sketchPlane" : qUnion([Q0])});
            skLineSegment(sketch, "E3", {"start": v(0, 14.3) * mm, "end": v(-7, 14.3) * mm});
            skLineSegment(sketch, "E4", {"start": v(-7, 14.3) * mm, "end": v(-7, 0) * mm});
            skLineSegment(sketch, "E5", {"start": v(-7, 0) * mm, "end": v(0, -4.42) * mm});
            skLineSegment(sketch, "E6", {"start": v(7, 0) * mm, "end": v(0, 4.22) * mm});
            skSolve(sketch);
        }
        {
            var Q0;
            {var subQ0=sQuery(id+"F2.wireOp",EDGE,"E3");Q0=makeQuery(id+"F2.imprint","IMPRINT",FACE,{"disambiguationData":[TD([[makeQuery(id+"F2.imprint","IMPRINT",EDGE,{"derivedFrom":subQ0}),1.0]])]});}
            extrude(context, id + "F3", {"entities" : qUnion([Q0]), "operationType" : NewBodyOperationType.ADD, "oppositeDirection" : true, "depth" : 9 * mm, "offsetDistance" : 25 * mm});
        }
        {
            var Q0;
            {var subQ0=sQuery(id+"F2.wireOp",EDGE,"E6");Q0=makeQuery(id+"F2.imprint","IMPRINT",FACE,{"disambiguationData":[TD([[makeQuery(id+"F2.imprint","IMPRINT",EDGE,{"derivedFrom":subQ0}),-1.0]])]});}
            extrude(context, id + "F4", {"entities" : qUnion([Q0]), "operationType" : NewBodyOperationType.REMOVE, "endBound" : BoundingType.THROUGH_ALL, "oppositeDirection" : true, "depth" : 25 * mm, "offsetDistance" : 25 * mm});
        }
        {
            var Q0;
            {var subQ0=sQuery(id+"F0.wireOp",EDGE,"E0.right");var subQ1=makeQuery(id+"F1.opExtrude","CAP_EDGE",EDGE,{"disambiguationData":[OSD([subQ0])],"isStart":true});Q0=makeQuery(id+"F4.boolean.opBoolean","COPY",FACE,{"derivedFrom":makeQuery(id+"F4.opExtrude","SWEPT_FACE",FACE,{"disambiguationData":[OSD([subQ0]),TDD([makeQuery(id+"F2.imprint","IMPRINT",EDGE,{"disambiguationData":[TD([[makeQuery(id+"F2.imprint","INTERSECT",VERTEX,{"derivedFrom":[subQ1,sQuery(id+"F2.wireOp",EDGE,"E6")]}),-1.0]])],"derivedFrom":subQ1})])]})});}
            var Q1;
            {var subQ0=sQuery(id+"F0.wireOp",EDGE,"E0.right");Q1=makeQuery(id+"F3.boolean.opBoolean","MERGE",FACE,{"derivedFrom":[makeQuery(id+"F1.opExtrude","SWEPT_FACE",FACE,{"disambiguationData":[OSD([subQ0])]}),makeQuery(id+"F3.opExtrude","CAP_FACE",FACE,{"disambiguationData":[OSD([subQ0,sQuery(id+"F2.wireOp",EDGE,"E3"),sQuery(id+"F2.wireOp",EDGE,"E4"),sQuery(id+"F2.wireOp",EDGE,"E5")])],"isStart":true})]});}
            var Q2;
            Q2=makeQuery(id+"F3.boolean.opBoolean","MERGE",FACE,{"derivedFrom":[makeQuery(id+"F1.opExtrude","SWEPT_FACE",FACE,{"disambiguationData":[OSD([sQuery(id+"F0.wireOp",EDGE,"E0.left")])]}),makeQuery(id+"F3.opExtrude","CAP_FACE",FACE,{"disambiguationData":[OSD([sQuery(id+"F0.wireOp",EDGE,"E0.right"),sQuery(id+"F2.wireOp",EDGE,"E3"),sQuery(id+"F2.wireOp",EDGE,"E4"),sQuery(id+"F2.wireOp",EDGE,"E5")])],"isStart":false})]});
            var Q3;
            Q3=makeQuery(id+"F3.opExtrude","SWEPT_FACE",FACE,{"disambiguationData":[OSD([sQuery(id+"F2.wireOp",EDGE,"E4")])]});
            var Q4;
            Q4=makeQuery(id+"F4.boolean.opBoolean","COPY",FACE,{"derivedFrom":makeQuery(id+"F4.opExtrude","SWEPT_FACE",FACE,{"disambiguationData":[OSD([sQuery(id+"F2.wireOp",EDGE,"E6")])]})});
            var Q5;
            Q5=makeQuery(id+"F3.opExtrude","SWEPT_FACE",FACE,{"disambiguationData":[OSD([sQuery(id+"F2.wireOp",EDGE,"E5")])]});
            fillet(context, id + "F5", {"entities" : qUnion([Q0, Q1, Q2, Q3, Q4, Q5]), "radius" : 1.3 * mm, "tangentPropagation" : true, "allowEdgeOverflow" : false});
        }
        {
            var Q0;
            Q0=makeQuery(id+"F3.boolean.opBoolean","MERGE",FACE,{"derivedFrom":[makeQuery(id+"F1.opExtrude","SWEPT_FACE",FACE,{"disambiguationData":[OSD([sQuery(id+"F0.wireOp",EDGE,"E0.top")])]}),makeQuery(id+"F3.opExtrude","SWEPT_FACE",FACE,{"disambiguationData":[OSD([sQuery(id+"F2.wireOp",EDGE,"E3")])]})]});
            var sketch = newSketch(context, id + "F6", { "sketchPlane" : qUnion([Q0])});
            skLineSegment(sketch, "E7.bottom", {"start": v(-1.53, -2.97) * mm, "end": v(-5.47, -2.97) * mm});
            skLineSegment(sketch, "E7.top", {"start": v(-1.53, -2.68) * mm, "end": v(-5.47, -2.68) * mm});
            skLineSegment(sketch, "E7.left", {"start": v(-1.53, -2.97) * mm, "end": v(-1.53, -2.68) * mm});
            skLineSegment(sketch, "E7.right", {"start": v(-5.47, -2.97) * mm, "end": v(-5.47, -2.68) * mm});
            skPoint(sketch, "E7.middle", {"position": v(-3.5, -2.82) * mm});
            skPoint(sketch, "E7.middle.positionSnap0", {"position": v(-3.5, -3.2) * mm});
            skPoint(sketch, "E7.centerSnap0", {"position": v(-3.5, -3.2) * mm});
            skLineSegment(sketch, "E8.0.1.0", {"start": v(-1.53, -2.46) * mm, "end": v(-1.53, -2.17) * mm});
            skLineSegment(sketch, "E8.0.1.1", {"start": v(-5.47, -2.46) * mm, "end": v(-5.47, -2.17) * mm});
            skLineSegment(sketch, "E8.0.1.2", {"start": v(-1.53, -2.46) * mm, "end": v(-5.47, -2.46) * mm});
            skLineSegment(sketch, "E8.0.1.3", {"start": v(-1.53, -2.17) * mm, "end": v(-5.47, -2.17) * mm});
            skLineSegment(sketch, "E8.0.2.0", {"start": v(-1.53, -1.95) * mm, "end": v(-1.53, -1.66) * mm});
            skLineSegment(sketch, "E8.0.2.1", {"start": v(-5.47, -1.95) * mm, "end": v(-5.47, -1.66) * mm});
            skLineSegment(sketch, "E8.0.2.2", {"start": v(-1.53, -1.95) * mm, "end": v(-5.47, -1.95) * mm});
            skLineSegment(sketch, "E8.0.2.3", {"start": v(-1.53, -1.66) * mm, "end": v(-5.47, -1.66) * mm});
            skLineSegment(sketch, "E8.0.3.0", {"start": v(-1.53, -1.44) * mm, "end": v(-1.53, -1.15) * mm});
            skLineSegment(sketch, "E8.0.3.1", {"start": v(-5.47, -1.44) * mm, "end": v(-5.47, -1.15) * mm});
            skLineSegment(sketch, "E8.0.3.2", {"start": v(-1.53, -1.44) * mm, "end": v(-5.47, -1.44) * mm});
            skLineSegment(sketch, "E8.0.3.3", {"start": v(-1.53, -1.15) * mm, "end": v(-5.47, -1.15) * mm});
            skLineSegment(sketch, "E8.0.4.0", {"start": v(-1.53, -0.93) * mm, "end": v(-1.53, -0.64) * mm});
            skLineSegment(sketch, "E8.0.4.1", {"start": v(-5.47, -0.93) * mm, "end": v(-5.47, -0.64) * mm});
            skLineSegment(sketch, "E8.0.4.2", {"start": v(-1.53, -0.93) * mm, "end": v(-5.47, -0.93) * mm});
            skLineSegment(sketch, "E8.0.4.3", {"start": v(-1.53, -0.64) * mm, "end": v(-5.47, -0.64) * mm});
            skLineSegment(sketch, "E8.0.5.0", {"start": v(-1.53, -0.42) * mm, "end": v(-1.53, -0.13) * mm});
            skLineSegment(sketch, "E8.0.5.1", {"start": v(-5.47, -0.42) * mm, "end": v(-5.47, -0.13) * mm});
            skLineSegment(sketch, "E8.0.5.2", {"start": v(-1.53, -0.42) * mm, "end": v(-5.47, -0.42) * mm});
            skLineSegment(sketch, "E8.0.5.3", {"start": v(-1.53, -0.13) * mm, "end": v(-5.47, -0.13) * mm});
            skLineSegment(sketch, "E8.0.6.0", {"start": v(-1.53, 0.1) * mm, "end": v(-1.53, 0.38) * mm});
            skLineSegment(sketch, "E8.0.6.1", {"start": v(-5.47, 0.1) * mm, "end": v(-5.47, 0.38) * mm});
            skLineSegment(sketch, "E8.0.6.2", {"start": v(-1.53, 0.1) * mm, "end": v(-5.47, 0.1) * mm});
            skLineSegment(sketch, "E8.0.6.3", {"start": v(-1.53, 0.38) * mm, "end": v(-5.47, 0.38) * mm});
            skLineSegment(sketch, "E8.0.7.0", {"start": v(-1.53, 0.6) * mm, "end": v(-1.53, 0.89) * mm});
            skLineSegment(sketch, "E8.0.7.1", {"start": v(-5.47, 0.6) * mm, "end": v(-5.47, 0.89) * mm});
            skLineSegment(sketch, "E8.0.7.2", {"start": v(-1.53, 0.6) * mm, "end": v(-5.47, 0.6) * mm});
            skLineSegment(sketch, "E8.0.7.3", {"start": v(-1.53, 0.89) * mm, "end": v(-5.47, 0.89) * mm});
            skLineSegment(sketch, "E8.0.8.0", {"start": v(-1.53, 1.11) * mm, "end": v(-1.53, 1.4) * mm});
            skLineSegment(sketch, "E8.0.8.1", {"start": v(-5.47, 1.11) * mm, "end": v(-5.47, 1.4) * mm});
            skLineSegment(sketch, "E8.0.8.2", {"start": v(-1.53, 1.11) * mm, "end": v(-5.47, 1.11) * mm});
            skLineSegment(sketch, "E8.0.8.3", {"start": v(-1.53, 1.4) * mm, "end": v(-5.47, 1.4) * mm});
            skLineSegment(sketch, "E8.0.9.0", {"start": v(-1.53, 1.62) * mm, "end": v(-1.53, 1.9) * mm});
            skLineSegment(sketch, "E8.0.9.1", {"start": v(-5.47, 1.62) * mm, "end": v(-5.47, 1.9) * mm});
            skLineSegment(sketch, "E8.0.9.2", {"start": v(-1.53, 1.62) * mm, "end": v(-5.47, 1.62) * mm});
            skLineSegment(sketch, "E8.0.9.3", {"start": v(-1.53, 1.9) * mm, "end": v(-5.47, 1.9) * mm});
            skLineSegment(sketch, "E8.0.10.0", {"start": v(-1.53, 2.13) * mm, "end": v(-1.53, 2.42) * mm});
            skLineSegment(sketch, "E8.0.10.1", {"start": v(-5.47, 2.13) * mm, "end": v(-5.47, 2.42) * mm});
            skLineSegment(sketch, "E8.0.10.2", {"start": v(-1.53, 2.13) * mm, "end": v(-5.47, 2.13) * mm});
            skLineSegment(sketch, "E8.0.10.3", {"start": v(-1.53, 2.42) * mm, "end": v(-5.47, 2.42) * mm});
            skLineSegment(sketch, "E8.0.11.0", {"start": v(-1.53, 2.64) * mm, "end": v(-1.53, 2.93) * mm});
            skLineSegment(sketch, "E8.0.11.1", {"start": v(-5.47, 2.64) * mm, "end": v(-5.47, 2.93) * mm});
            skLineSegment(sketch, "E8.0.11.2", {"start": v(-1.53, 2.64) * mm, "end": v(-5.47, 2.64) * mm});
            skLineSegment(sketch, "E8.0.11.3", {"start": v(-1.53, 2.93) * mm, "end": v(-5.47, 2.93) * mm});
            skLineSegment(sketch, "E8.2.0.0", {"start": v(48.47, -2.97) * mm, "end": v(48.47, -2.68) * mm});
            skLineSegment(sketch, "E8.2.0.1", {"start": v(44.53, -2.97) * mm, "end": v(44.53, -2.68) * mm});
            skLineSegment(sketch, "E8.2.0.2", {"start": v(48.47, -2.97) * mm, "end": v(44.53, -2.97) * mm});
            skLineSegment(sketch, "E8.2.0.3", {"start": v(48.47, -2.68) * mm, "end": v(44.53, -2.68) * mm});
            skLineSegment(sketch, "E8.2.1.0", {"start": v(48.47, -2.46) * mm, "end": v(48.47, -2.17) * mm});
            skLineSegment(sketch, "E8.2.1.1", {"start": v(44.53, -2.46) * mm, "end": v(44.53, -2.17) * mm});
            skLineSegment(sketch, "E8.2.1.2", {"start": v(48.47, -2.46) * mm, "end": v(44.53, -2.46) * mm});
            skLineSegment(sketch, "E8.2.1.3", {"start": v(48.47, -2.17) * mm, "end": v(44.53, -2.17) * mm});
            skLineSegment(sketch, "E8.2.2.0", {"start": v(48.47, -1.95) * mm, "end": v(48.47, -1.66) * mm});
            skLineSegment(sketch, "E8.2.2.1", {"start": v(44.53, -1.95) * mm, "end": v(44.53, -1.66) * mm});
            skLineSegment(sketch, "E8.2.2.2", {"start": v(48.47, -1.95) * mm, "end": v(44.53, -1.95) * mm});
            skLineSegment(sketch, "E8.2.2.3", {"start": v(48.47, -1.66) * mm, "end": v(44.53, -1.66) * mm});
            skLineSegment(sketch, "E8.2.3.0", {"start": v(48.47, -1.44) * mm, "end": v(48.47, -1.15) * mm});
            skLineSegment(sketch, "E8.2.3.1", {"start": v(44.53, -1.44) * mm, "end": v(44.53, -1.15) * mm});
            skLineSegment(sketch, "E8.2.3.2", {"start": v(48.47, -1.44) * mm, "end": v(44.53, -1.44) * mm});
            skLineSegment(sketch, "E8.2.3.3", {"start": v(48.47, -1.15) * mm, "end": v(44.53, -1.15) * mm});
            skLineSegment(sketch, "E8.2.4.0", {"start": v(48.47, -0.93) * mm, "end": v(48.47, -0.64) * mm});
            skLineSegment(sketch, "E8.2.4.1", {"start": v(44.53, -0.93) * mm, "end": v(44.53, -0.64) * mm});
            skLineSegment(sketch, "E8.2.4.2", {"start": v(48.47, -0.93) * mm, "end": v(44.53, -0.93) * mm});
            skLineSegment(sketch, "E8.2.4.3", {"start": v(48.47, -0.64) * mm, "end": v(44.53, -0.64) * mm});
            skLineSegment(sketch, "E8.2.5.0", {"start": v(48.47, -0.42) * mm, "end": v(48.47, -0.13) * mm});
            skLineSegment(sketch, "E8.2.5.1", {"start": v(44.53, -0.42) * mm, "end": v(44.53, -0.13) * mm});
            skLineSegment(sketch, "E8.2.5.2", {"start": v(48.47, -0.42) * mm, "end": v(44.53, -0.42) * mm});
            skLineSegment(sketch, "E8.2.5.3", {"start": v(48.47, -0.13) * mm, "end": v(44.53, -0.13) * mm});
            skLineSegment(sketch, "E8.2.6.0", {"start": v(48.47, 0.1) * mm, "end": v(48.47, 0.38) * mm});
            skLineSegment(sketch, "E8.2.6.1", {"start": v(44.53, 0.1) * mm, "end": v(44.53, 0.38) * mm});
            skLineSegment(sketch, "E8.2.6.2", {"start": v(48.47, 0.1) * mm, "end": v(44.53, 0.1) * mm});
            skLineSegment(sketch, "E8.2.6.3", {"start": v(48.47, 0.38) * mm, "end": v(44.53, 0.38) * mm});
            skLineSegment(sketch, "E8.2.7.0", {"start": v(48.47, 0.6) * mm, "end": v(48.47, 0.89) * mm});
            skLineSegment(sketch, "E8.2.7.1", {"start": v(44.53, 0.6) * mm, "end": v(44.53, 0.89) * mm});
            skLineSegment(sketch, "E8.2.7.2", {"start": v(48.47, 0.6) * mm, "end": v(44.53, 0.6) * mm});
            skLineSegment(sketch, "E8.2.7.3", {"start": v(48.47, 0.89) * mm, "end": v(44.53, 0.89) * mm});
            skLineSegment(sketch, "E8.2.8.0", {"start": v(48.47, 1.11) * mm, "end": v(48.47, 1.4) * mm});
            skLineSegment(sketch, "E8.2.8.1", {"start": v(44.53, 1.11) * mm, "end": v(44.53, 1.4) * mm});
            skLineSegment(sketch, "E8.2.8.2", {"start": v(48.47, 1.11) * mm, "end": v(44.53, 1.11) * mm});
            skLineSegment(sketch, "E8.2.8.3", {"start": v(48.47, 1.4) * mm, "end": v(44.53, 1.4) * mm});
            skLineSegment(sketch, "E8.2.9.0", {"start": v(48.47, 1.62) * mm, "end": v(48.47, 1.9) * mm});
            skLineSegment(sketch, "E8.2.9.1", {"start": v(44.53, 1.62) * mm, "end": v(44.53, 1.9) * mm});
            skLineSegment(sketch, "E8.2.9.2", {"start": v(48.47, 1.62) * mm, "end": v(44.53, 1.62) * mm});
            skLineSegment(sketch, "E8.2.9.3", {"start": v(48.47, 1.9) * mm, "end": v(44.53, 1.9) * mm});
            skLineSegment(sketch, "E8.2.10.0", {"start": v(48.47, 2.13) * mm, "end": v(48.47, 2.42) * mm});
            skLineSegment(sketch, "E8.2.10.1", {"start": v(44.53, 2.13) * mm, "end": v(44.53, 2.42) * mm});
            skLineSegment(sketch, "E8.2.10.2", {"start": v(48.47, 2.13) * mm, "end": v(44.53, 2.13) * mm});
            skLineSegment(sketch, "E8.2.10.3", {"start": v(48.47, 2.42) * mm, "end": v(44.53, 2.42) * mm});
            skLineSegment(sketch, "E8.2.11.0", {"start": v(48.47, 2.64) * mm, "end": v(48.47, 2.93) * mm});
            skLineSegment(sketch, "E8.2.11.1", {"start": v(44.53, 2.64) * mm, "end": v(44.53, 2.93) * mm});
            skLineSegment(sketch, "E8.2.11.2", {"start": v(48.47, 2.64) * mm, "end": v(44.53, 2.64) * mm});
            skLineSegment(sketch, "E8.2.11.3", {"start": v(48.47, 2.93) * mm, "end": v(44.53, 2.93) * mm});
            skLineSegment(sketch, "E8.direction1", {"start": v(-5.47, -2.97) * mm, "end": v(19.53, -2.97) * mm, "construction": true});
            skLineSegment(sketch, "E8.direction2", {"start": v(-5.47, -2.97) * mm, "end": v(-5.47, -2.46) * mm, "construction": true});
            skSolve(sketch);
        }
        {
            var Q0;
            Q0=makeQuery(id+"F6.imprint","IMPRINT",FACE,{"disambiguationData":[TD([[makeQuery(id+"F6.imprint","IMPRINT",EDGE,{"derivedFrom":sQuery(id+"F6.wireOp",EDGE,"E8.2.10.0")}),1.0]])]});
            var Q1;
            Q1=makeQuery(id+"F6.imprint","IMPRINT",FACE,{"disambiguationData":[TD([[makeQuery(id+"F6.imprint","IMPRINT",EDGE,{"derivedFrom":sQuery(id+"F6.wireOp",EDGE,"E8.2.6.0")}),1.0]])]});
            var Q2;
            Q2=makeQuery(id+"F6.imprint","IMPRINT",FACE,{"disambiguationData":[TD([[makeQuery(id+"F6.imprint","IMPRINT",EDGE,{"derivedFrom":sQuery(id+"F6.wireOp",EDGE,"E8.2.2.0")}),1.0]])]});
            var Q3;
            Q3=makeQuery(id+"F6.imprint","IMPRINT",FACE,{"disambiguationData":[TD([[makeQuery(id+"F6.imprint","IMPRINT",EDGE,{"derivedFrom":sQuery(id+"F6.wireOp",EDGE,"E8.2.7.0")}),1.0]])]});
            var Q4;
            Q4=makeQuery(id+"F6.imprint","IMPRINT",FACE,{"disambiguationData":[TD([[makeQuery(id+"F6.imprint","IMPRINT",EDGE,{"derivedFrom":sQuery(id+"F6.wireOp",EDGE,"E8.2.8.0")}),1.0]])]});
            var Q5;
            Q5=makeQuery(id+"F6.imprint","IMPRINT",FACE,{"disambiguationData":[TD([[makeQuery(id+"F6.imprint","IMPRINT",EDGE,{"derivedFrom":sQuery(id+"F6.wireOp",EDGE,"E8.2.1.0")}),1.0]])]});
            var Q6;
            Q6=makeQuery(id+"F6.imprint","IMPRINT",FACE,{"disambiguationData":[TD([[makeQuery(id+"F6.imprint","IMPRINT",EDGE,{"derivedFrom":sQuery(id+"F6.wireOp",EDGE,"E8.2.11.0")}),1.0]])]});
            var Q7;
            Q7=makeQuery(id+"F6.imprint","IMPRINT",FACE,{"disambiguationData":[TD([[makeQuery(id+"F6.imprint","IMPRINT",EDGE,{"derivedFrom":sQuery(id+"F6.wireOp",EDGE,"E8.2.5.0")}),1.0]])]});
            var Q8;
            Q8=makeQuery(id+"F6.imprint","IMPRINT",FACE,{"disambiguationData":[TD([[makeQuery(id+"F6.imprint","IMPRINT",EDGE,{"derivedFrom":sQuery(id+"F6.wireOp",EDGE,"E8.2.3.0")}),1.0]])]});
            var Q9;
            Q9=makeQuery(id+"F6.imprint","IMPRINT",FACE,{"disambiguationData":[TD([[makeQuery(id+"F6.imprint","IMPRINT",EDGE,{"derivedFrom":sQuery(id+"F6.wireOp",EDGE,"E8.2.9.0")}),1.0]])]});
            var Q10;
            Q10=makeQuery(id+"F6.imprint","IMPRINT",FACE,{"disambiguationData":[TD([[makeQuery(id+"F6.imprint","IMPRINT",EDGE,{"derivedFrom":sQuery(id+"F6.wireOp",EDGE,"E8.2.4.0")}),1.0]])]});
            var Q11;
            Q11=makeQuery(id+"F6.imprint","IMPRINT",FACE,{"disambiguationData":[TD([[makeQuery(id+"F6.imprint","IMPRINT",EDGE,{"derivedFrom":sQuery(id+"F6.wireOp",EDGE,"E8.2.0.0")}),1.0]])]});
            var Q12;
            Q12=makeQuery(id+"F6.imprint","IMPRINT",FACE,{"disambiguationData":[TD([[makeQuery(id+"F6.imprint","IMPRINT",EDGE,{"derivedFrom":sQuery(id+"F6.wireOp",EDGE,"E7.bottom")}),1.0]])]});
            extrude(context, id + "F7", {"entities" : qUnion([Q0, Q1, Q2, Q3, Q4, Q5, Q6, Q7, Q8, Q9, Q10, Q11, Q12]), "operationType" : NewBodyOperationType.REMOVE, "oppositeDirection" : true, "depth" : 0.5 * mm, "offsetDistance" : 25 * mm});
        }
    });
